# Revit family: Building-ConnessioniIEC309-GEWISS-67IB-PRESE-INTERBLOCCATE_IP67_CON_FONDO_63A
name_source: partatom
category: Apparecchi elettrici
units: mm (PartAtom-declared; Revit-internal decimal feet)

## family parameters
Condiviso = Sì
Host = Superficie
Mantenere orientamento annotazione = Sì
Punto di calcolo locali = Sì
Quota connettore circolare = Usa diametro
Taglio con vuoti quando caricato = Sì
Tipo di parte = Normale

## types (11) — shared parameters
Catalogo = BUILDING
Catalogo Serie = 67 IB
Codice Electrocod = 2222
Con fondo = Si
Corpo presa = GEWISS -BLU
Corrente nominale (A) = 63
Corrente nominale (In) = 63
Frequenza = 50/60 Hz
Frequenza nominale (Hz) = 50/60 Hz
Glow Wire Test = 850 °C (Presa IB) - 650 °C (Cassetta di fondo)
Glow wire test: = 850 °C (Presa IB) - 650 °C (Cassetta di fondo)
Grado di protezione = IP67
IDF = 5cabc3db-9b0e-4f85-a9f2-ad60fda3b60e
IDT = a25d3694-d0a1-482b-9cd4-b67b9b60fa6b
Immagine tipo = F.jpg
Produttore = GEWISS S.p.A.
Prospetto di default = 1219 mm
Protezione = NO (SBF)
Resistenza agli urti = IK08
SEO = Presa
Scheda Tecnica = https://www.gewiss.com
Simbolo presa = PRESAINDSTAGNA : 3P
Struttura = Grigio RAL - 7035
Temperatura di funzionamento = -25 ÷ +40 °C
Temperatura di utilizzo = -25 +40 °C
Termopressione con biglia = 125 °C (Presa IB) - 80 °C (Cassetta di fondo)
Tipologia = Verticale
URL = https://www.gewiss.com
Versione file RFA = 21.4
presa = Giallo
zero-valued in all types: giallo

## per-type parameters (varying)
| type | Codice EAN | Colore | Colore: | Descrizione | Modello | N. poli | Numero di poli | Riferimento h | Tensione nominale | Tensione nominale: |
| GW67260N - PR.BL IP67 C.F.3P+T 63A 230V 9H SBF | 8011564742307 | Blu | Blu | PR.BL IP67 C.F.3P+T 63A 230V 9H SBF | GW67260N | 3P+T | 3P+T | 9 | 200 - 250 V | 200 - 250 V |
| GW67262N - PR.BL IP67 C.F.2P+T 63A 400V 9H SBF | 8011564742321 | Rosso | Rosso | PR.BL IP67 C.F.2P+T 63A 400V 9H SBF | GW67262N | 2P+T | 2P+T | 9 | 380 - 415 V | 380 - 415 V |
| GW67266N - PR.BL IP67 C.F.3P+N+T 63A 500V 7H SBF | 8011564742369 | Nero | Nero | PR.BL IP67 C.F.3P+N+T 63A 500V 7H SBF | GW67266N | 3P+N+T | 3P+N+T | 7 | 480 - 500 V | 480 - 500 V |
| GW67257N - PR.BL IP67 C.F.3P+T 63A 110V 4H SBF | 8011564742277 | Giallo | Giallo | PR.BL IP67 C.F.3P+T 63A 110V 4H SBF | GW67257N | 3P+T | 3P+T | 4 | 100 - 130 V | 100 - 130 V |
| GW67258N - PR.BL IP67 C.F.3P+N+T 63A 110V 4H SBF | 8011564742284 | Giallo | Giallo | PR.BL IP67 C.F.3P+N+T 63A 110V 4H SBF | GW67258N | 3P+N+T | 3P+N+T | 4 | 100 - 130 V | 100 - 130 V |
| GW67256N - PR.BL IP67 C.F.2P+T 63A 110V 4H SBF | 8011564742260 | Giallo | Giallo | PR.BL IP67 C.F.2P+T 63A 110V 4H SBF | GW67256N | 2P+T | 2P+T | 4 | 100 - 130 V | 100 - 130 V |
| GW67263N - PR.BL IP67 C.F.3P+T 63A 400V 6H SBF | 8011564742338 | Rosso | Rosso | PR.BL IP67 C.F.3P+T 63A 400V 6H SBF | GW67263N | 3P+T | 3P+T | 6 | 380 - 415 V | 380 - 415 V |
| GW67265N - PR.BL IP67 C.F.3P+T 63A 500V 7H SBF | 8011564742352 | Nero | Nero | PR.BL IP67 C.F.3P+T 63A 500V 7H SBF | GW67265N | 3P+T | 3P+T | 7 | 480 - 500 V | 480 - 500 V |
| GW67264N - PR.BL IP67 C.F.3P+N+T 63A 400V 6H SBF | 8011564742345 | Rosso | Rosso | PR.BL IP67 C.F.3P+N+T 63A 400V 6H SBF | GW67264N | 3P+N+T | 3P+N+T | 6 | 380 - 415 V | 380 - 415 V |
| GW67261N - PR.BL IP67 C.F.3P+N+T 63A 230V 9H SBF | 8011564742314 | Blu | Blu | PR.BL IP67 C.F.3P+N+T 63A 230V 9H SBF | GW67261N | 3P+N+T | 3P+N+T | 9 | 200 - 250 V | 200 - 250 V |
| GW67259N - PR.BL IP67 C.F.2P+T 63A 230V 6H SBF | 8011564742291 | Blu | Blu | PR.BL IP67 C.F.2P+T 63A 230V 6H SBF | GW67259N | 2P+T | 2P+T | 6 | 200 - 250 V | 200 - 250 V |

## geometry (parser evidence)
native form markers: Sweep x4
no freeform markers — native parametric forms only
